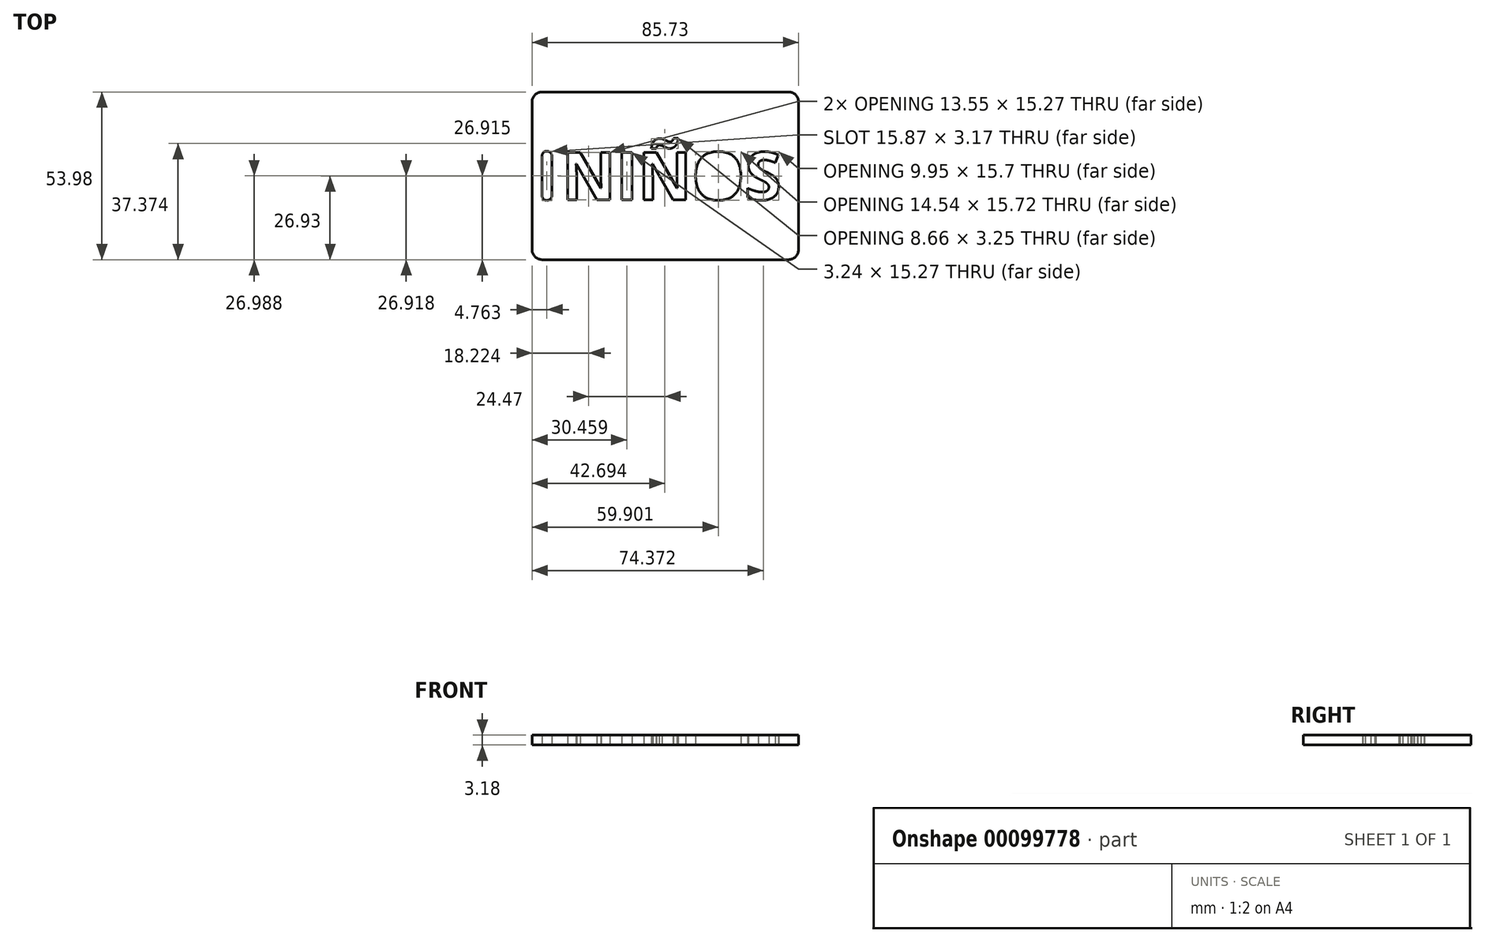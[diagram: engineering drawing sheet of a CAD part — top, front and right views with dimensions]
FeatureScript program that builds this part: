
annotation { "Feature Type Name" : "Feature", "Feature Type Description" : "" }
export const myFeature = defineFeature(function(context is Context, id is Id, definition is map)
    precondition{}
    {
        {
            var Q0;
            Q0=qCreatedBy(makeId("Top.planeOp"),FACE);
            var sketch = newSketch(context, id + "F0", { "sketchPlane" : qUnion([Q0])});
            skLineSegment(sketch, "E0.bottom", {"start": v(3.17, 0) * mm, "end": v(82.55, 0) * mm});
            skLineSegment(sketch, "E0.top", {"start": v(3.17, 53.98) * mm, "end": v(82.55, 53.97) * mm});
            skLineSegment(sketch, "E0.left", {"start": v(0, 3.18) * mm, "end": v(0, 50.8) * mm});
            skLineSegment(sketch, "E0.right", {"start": v(85.73, 3.18) * mm, "end": v(85.73, 50.8) * mm});
            skPoint(sketch, "E1.visualSharp", {"position": v(0, 53.98) * mm});
            skArc(sketch, "E1.filletArc", {"start": v(3.17, 53.98) * mm, "mid": v(0.93, 53.05) * mm, "end": v(0, 50.8) * mm});
            skPoint(sketch, "E2.visualSharp", {"position": v(85.73, 53.97) * mm});
            skArc(sketch, "E2.filletArc", {"start": v(85.73, 50.8) * mm, "mid": v(84.8, 53.05) * mm, "end": v(82.55, 53.97) * mm});
            skPoint(sketch, "E3.visualSharp", {"position": v(85.73, 0) * mm});
            skArc(sketch, "E3.filletArc", {"start": v(82.55, 0) * mm, "mid": v(84.8, 0.93) * mm, "end": v(85.73, 3.18) * mm});
            skPoint(sketch, "E4.visualSharp", {"position": v(0, 0) * mm});
            skArc(sketch, "E4.filletArc", {"start": v(0, 3.18) * mm, "mid": v(0.93, 0.93) * mm, "end": v(3.17, 0) * mm});
            skLineSegment(sketch, "E5", {"start": v(3.17, 33.34) * mm, "end": v(3.17, 20.64) * mm});
            skLineSegment(sketch, "E6", {"start": v(6.35, 33.34) * mm, "end": v(6.35, 20.64) * mm});
            skLineSegment(sketch, "E7", {"start": v(0, 26.99) * mm, "end": v(3.17, 26.99) * mm});
            skPoint(sketch, "E7.endSnap0", {"position": v(0, 26.99) * mm});
            skArc(sketch, "E8", {"start": v(6.35, 33.34) * mm, "mid": v(4.76, 34.93) * mm, "end": v(3.17, 33.34) * mm});
            skArc(sketch, "E9", {"start": v(3.17, 20.64) * mm, "mid": v(4.76, 19.05) * mm, "end": v(6.35, 20.64) * mm});
            skText(sketch, "E10", { "text": "NIÑOS", "fontName": "OpenSans-Bold.ttf"});
            skLineSegment(sketch, "E11", {"start": v(6.35, 26.99) * mm, "end": v(9.52, 26.99) * mm});
            const initialGuessF0  = {"E10": [0.00953, 0.01928, 1, 0, 0.0154]};
            skSetInitialGuess(sketch, initialGuessF0);
            skSolve(sketch);
        }
        {
            var Q0;
            Q0=makeQuery(id+"F0.imprint","IMPRINT",FACE,{"disambiguationData":[TD([[makeQuery(id+"F0.imprint","IMPRINT",EDGE,{"derivedFrom":sQuery(id+"F0.wireOp",EDGE,"E0.bottom")}),1.0]])]});
            extrude(context, id + "F1", {"entities" : qUnion([Q0]), "depth" : 3.17 * mm});
        }
    });
